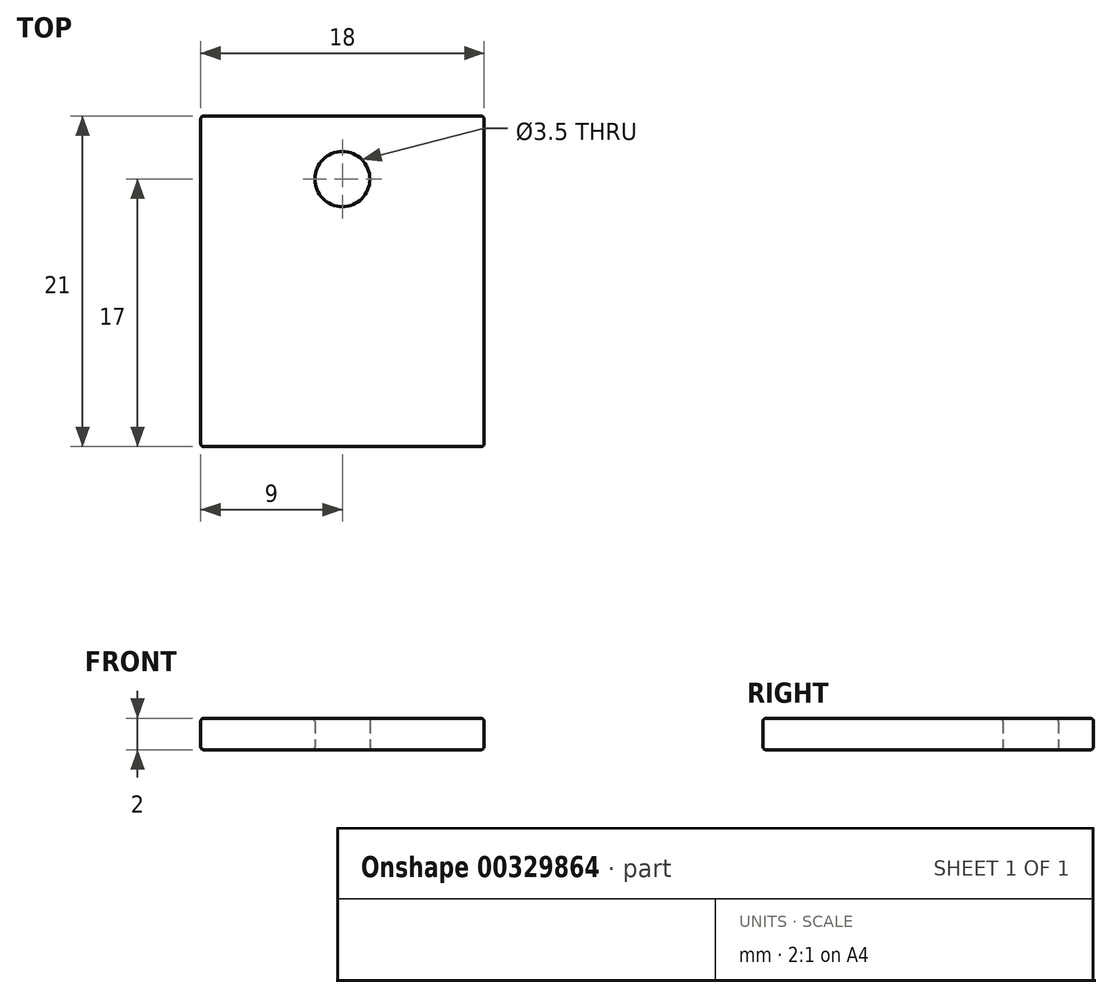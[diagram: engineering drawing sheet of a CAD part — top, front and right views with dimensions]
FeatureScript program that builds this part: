
annotation { "Feature Type Name" : "Feature", "Feature Type Description" : "" }
export const myFeature = defineFeature(function(context is Context, id is Id, definition is map)
    precondition{}
    {
        {
            var Q0;
            Q0=qCreatedBy(makeId("Top.planeOp"),FACE);
            var sketch = newSketch(context, id + "F0", { "sketchPlane" : qUnion([Q0])});
            skLineSegment(sketch, "E0.bottom", {"start": v(0, 0) * mm, "end": v(18, 0) * mm});
            skLineSegment(sketch, "E0.top", {"start": v(0, 21) * mm, "end": v(18, 21) * mm});
            skLineSegment(sketch, "E0.left", {"start": v(0, 0) * mm, "end": v(0, 21) * mm});
            skLineSegment(sketch, "E0.right", {"start": v(18, 0) * mm, "end": v(18, 21) * mm});
            skCircle(sketch, "E1", {"center": v(9, 17) * mm, "radius": 1.75 * mm});
            skPoint(sketch, "E1.centerSnap0", {"position": v(9, 21) * mm});
            skPoint(sketch, "E2.centerSnap0", {"position": v(9, 0) * mm});
            skSolve(sketch);
        }
        {
            var Q0;
            Q0 = qSketchRegion(id + "F0", true);
            extrude(context, id + "F1", {"entities" : qUnion([Q0]), "depth" : 2 * mm, "offsetDistance" : 25 * mm});
        }
        {
            var Q0;
            Q0=makeQuery(id+"F1.opExtrude","CAP_FACE",FACE,{"disambiguationData":[OSD([sQuery(id+"F0.wireOp",EDGE,"E0.bottom"),sQuery(id+"F0.wireOp",EDGE,"E0.top"),sQuery(id+"F0.wireOp",EDGE,"E0.left"),sQuery(id+"F0.wireOp",EDGE,"E0.right"),sQuery(id+"F0.wireOp",EDGE,"E1")])],"isStart":false});
            var Q1;
            Q1=makeQuery(id+"F1.opExtrude","CAP_FACE",FACE,{"disambiguationData":[OSD([sQuery(id+"F0.wireOp",EDGE,"E0.bottom"),sQuery(id+"F0.wireOp",EDGE,"E0.top"),sQuery(id+"F0.wireOp",EDGE,"E0.left"),sQuery(id+"F0.wireOp",EDGE,"E0.right"),sQuery(id+"F0.wireOp",EDGE,"E1")])],"isStart":true});
            var Q2;
            Q2=makeQuery(id+"F1.opExtrude","SWEPT_FACE",FACE,{"disambiguationData":[OSD([sQuery(id+"F0.wireOp",EDGE,"E0.left")])]});
            var Q3;
            Q3=makeQuery(id+"F1.opExtrude","SWEPT_FACE",FACE,{"disambiguationData":[OSD([sQuery(id+"F0.wireOp",EDGE,"E0.bottom")])]});
            var Q4;
            Q4=makeQuery(id+"F1.opExtrude","SWEPT_FACE",FACE,{"disambiguationData":[OSD([sQuery(id+"F0.wireOp",EDGE,"E0.right")])]});
            var Q5;
            Q5=makeQuery(id+"F1.opExtrude","SWEPT_FACE",FACE,{"disambiguationData":[OSD([sQuery(id+"F0.wireOp",EDGE,"E0.top")])]});
            fillet(context, id + "F2", {"entities" : qUnion([Q0, Q1, Q2, Q3, Q4, Q5]), "tangentPropagation" : true, "radius" : 0.2 * mm, "defaultsChanged" : false, "vertexSettings" : [], "allowEdgeOverflow" : false});
        }
    });
